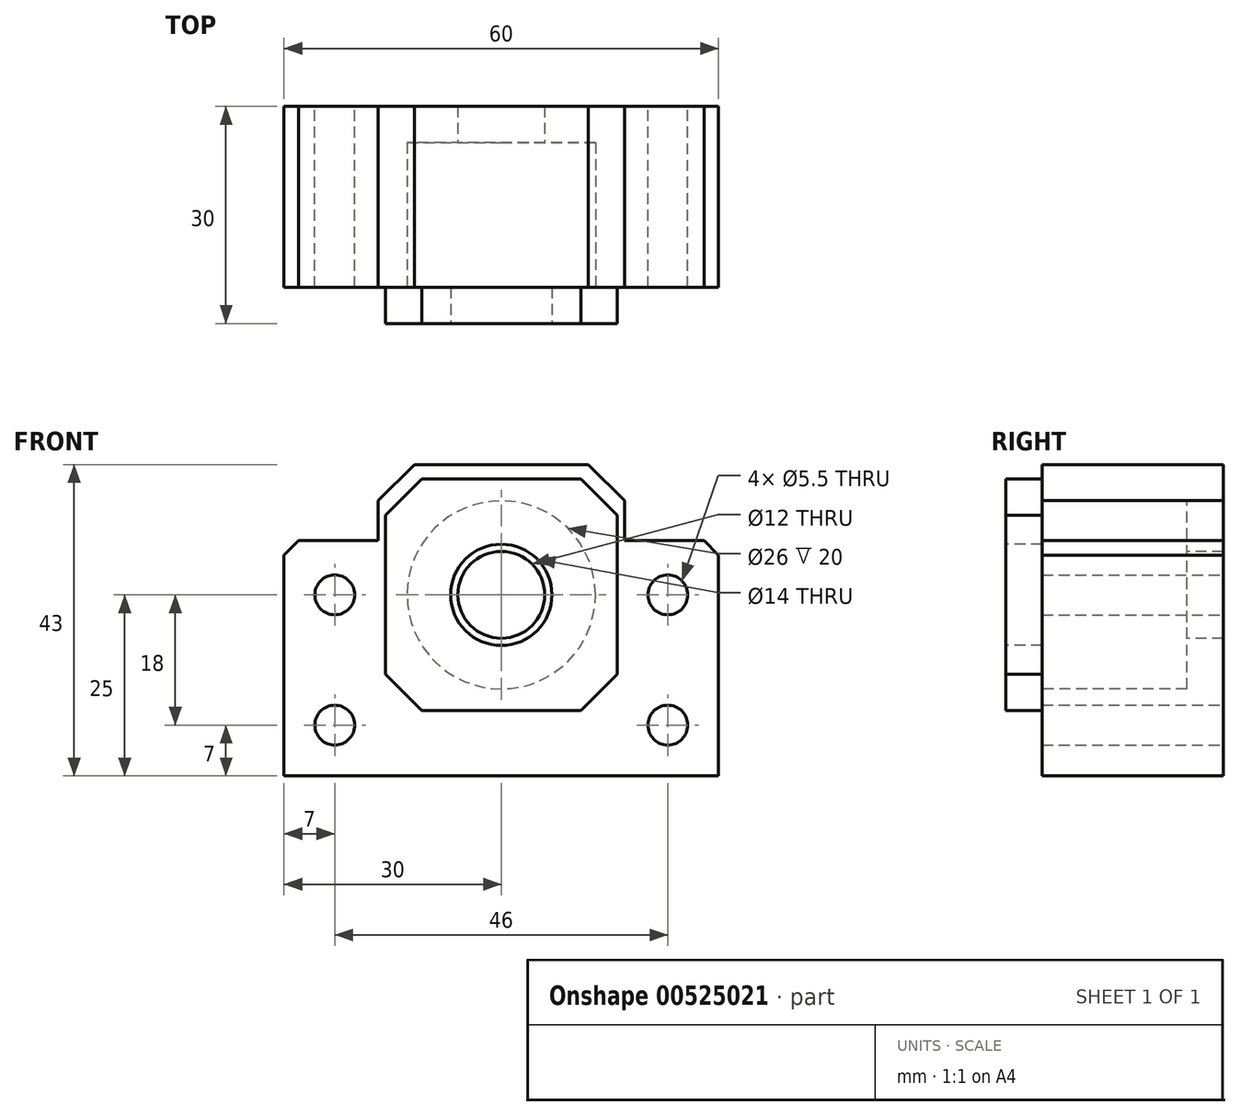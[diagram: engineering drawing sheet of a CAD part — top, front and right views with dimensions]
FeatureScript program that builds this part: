
annotation { "Feature Type Name" : "Feature", "Feature Type Description" : "" }
export const myFeature = defineFeature(function(context is Context, id is Id, definition is map)
    precondition{}
    {
        {
            var Q0;
            Q0=qCreatedBy(makeId("Front.planeOp"),FACE);
            var sketch = newSketch(context, id + "F0", { "sketchPlane" : qUnion([Q0])});
            skLineSegment(sketch, "E0.bottom", {"start": v(17, 21.5) * mm, "end": v(-17, 21.5) * mm});
            skLineSegment(sketch, "E0.top", {"start": v(30, -21.5) * mm, "end": v(-30, -21.5) * mm});
            skLineSegment(sketch, "E0.left", {"start": v(30, 11) * mm, "end": v(30, -21.5) * mm});
            skLineSegment(sketch, "E0.right", {"start": v(-30, 11) * mm, "end": v(-30, -21.5) * mm});
            skPoint(sketch, "E0.middle", {"position": v(0, 0) * mm});
            skLineSegment(sketch, "E1", {"start": v(-17, 21.5) * mm, "end": v(-17, 11) * mm});
            skLineSegment(sketch, "E2", {"start": v(-17, 11) * mm, "end": v(-30, 11) * mm});
            skLineSegment(sketch, "E3", {"start": v(17, 21.5) * mm, "end": v(17, 11) * mm});
            skLineSegment(sketch, "E4", {"start": v(17, 11) * mm, "end": v(30, 11) * mm});
            skPoint(sketch, "E5.orphan", {"position": v(-30, 21.5) * mm});
            skPoint(sketch, "E6.orphan", {"position": v(30, 21.5) * mm});
            skSolve(sketch);
        }
        {
            var Q0;
            Q0 = qSketchRegion(id + "F0", true);
            extrude(context, id + "F1", {"entities" : qUnion([Q0]), "endBound" : BoundingType.SYMMETRIC, "depth" : 25 * mm, "offsetDistance" : 25 * mm});
        }
        {
            var Q0;
            Q0=makeQuery(id+"F1.opExtrude","CAP_FACE",FACE,{"disambiguationData":[OSD([sQuery(id+"F0.wireOp",EDGE,"E0.bottom"),sQuery(id+"F0.wireOp",EDGE,"E0.top"),sQuery(id+"F0.wireOp",EDGE,"E0.left"),sQuery(id+"F0.wireOp",EDGE,"E0.right"),sQuery(id+"F0.wireOp",EDGE,"E1"),sQuery(id+"F0.wireOp",EDGE,"E2"),sQuery(id+"F0.wireOp",EDGE,"E3"),sQuery(id+"F0.wireOp",EDGE,"E4")])],"isStart":false});
            var sketch = newSketch(context, id + "F2", { "sketchPlane" : qUnion([Q0])});
            skCircle(sketch, "E7", {"center": v(0, 3.5) * mm, "radius": 6 * mm});
            skSolve(sketch);
        }
        {
            var Q0;
            Q0 = qSketchRegion(id + "F2", true);
            extrude(context, id + "F3", {"entities" : qUnion([Q0]), "operationType" : NewBodyOperationType.REMOVE, "oppositeDirection" : true, "depth" : 25 * mm, "offsetDistance" : 25 * mm});
        }
        {
            var Q0;
            Q0=makeQuery(id+"F1.opExtrude","CAP_FACE",FACE,{"disambiguationData":[OSD([sQuery(id+"F0.wireOp",EDGE,"E0.bottom"),sQuery(id+"F0.wireOp",EDGE,"E0.top"),sQuery(id+"F0.wireOp",EDGE,"E0.left"),sQuery(id+"F0.wireOp",EDGE,"E0.right"),sQuery(id+"F0.wireOp",EDGE,"E1"),sQuery(id+"F0.wireOp",EDGE,"E2"),sQuery(id+"F0.wireOp",EDGE,"E3"),sQuery(id+"F0.wireOp",EDGE,"E4")])],"isStart":false});
            var sketch = newSketch(context, id + "F4", { "sketchPlane" : qUnion([Q0])});
            skCircle(sketch, "E8", {"center": v(0, 3.5) * mm, "radius": 13 * mm});
            skSolve(sketch);
        }
        {
            var Q0;
            Q0 = qSketchRegion(id + "F4", true);
            extrude(context, id + "F5", {"entities" : qUnion([Q0]), "operationType" : NewBodyOperationType.REMOVE, "oppositeDirection" : true, "depth" : 20 * mm, "offsetDistance" : 25 * mm});
        }
        {
            var Q0;
            Q0=makeQuery(id+"F1.opExtrude","CAP_FACE",FACE,{"disambiguationData":[OSD([sQuery(id+"F0.wireOp",EDGE,"E0.bottom"),sQuery(id+"F0.wireOp",EDGE,"E0.top"),sQuery(id+"F0.wireOp",EDGE,"E0.left"),sQuery(id+"F0.wireOp",EDGE,"E0.right"),sQuery(id+"F0.wireOp",EDGE,"E1"),sQuery(id+"F0.wireOp",EDGE,"E2"),sQuery(id+"F0.wireOp",EDGE,"E3"),sQuery(id+"F0.wireOp",EDGE,"E4")])],"isStart":false});
            var sketch = newSketch(context, id + "F6", { "sketchPlane" : qUnion([Q0])});
            skLineSegment(sketch, "E9.bottom", {"start": v(16, -12.5) * mm, "end": v(-16, -12.5) * mm});
            skLineSegment(sketch, "E9.top", {"start": v(16, 19.5) * mm, "end": v(-16, 19.5) * mm});
            skLineSegment(sketch, "E9.left", {"start": v(16, -12.5) * mm, "end": v(16, 19.5) * mm});
            skLineSegment(sketch, "E9.right", {"start": v(-16, -12.5) * mm, "end": v(-16, 19.5) * mm});
            skPoint(sketch, "E9.middle", {"position": v(0, 3.5) * mm});
            skSolve(sketch);
        }
        {
            var Q0;
            Q0 = qSketchRegion(id + "F6", true);
            extrude(context, id + "F7", {"entities" : qUnion([Q0]), "operationType" : NewBodyOperationType.ADD, "depth" : 5 * mm, "offsetDistance" : 25 * mm});
        }
        {
            var Q0;
            Q0=makeQuery(id+"F7.opExtrude","CAP_FACE",FACE,{"disambiguationData":[OSD([sQuery(id+"F6.wireOp",EDGE,"E9.bottom"),sQuery(id+"F6.wireOp",EDGE,"E9.top"),sQuery(id+"F6.wireOp",EDGE,"E9.left"),sQuery(id+"F6.wireOp",EDGE,"E9.right")])],"isStart":false});
            var sketch = newSketch(context, id + "F8", { "sketchPlane" : qUnion([Q0])});
            skCircle(sketch, "E10", {"center": v(0, 3.5) * mm, "radius": 7 * mm});
            skSolve(sketch);
        }
        {
            var Q0;
            Q0 = qSketchRegion(id + "F8", true);
            extrude(context, id + "F9", {"entities" : qUnion([Q0]), "operationType" : NewBodyOperationType.REMOVE, "oppositeDirection" : true, "depth" : 5 * mm, "offsetDistance" : 25 * mm});
        }
        {
            var Q0;
            Q0=makeQuery(id+"F7.opExtrude","SWEPT_EDGE",EDGE,{"disambiguationData":[OSD([sQuery(id+"F6.wireOp",EDGE,"E9.top"),sQuery(id+"F6.wireOp",EDGE,"E9.right")])]});
            var Q1;
            Q1=makeQuery(id+"F7.opExtrude","SWEPT_EDGE",EDGE,{"disambiguationData":[OSD([sQuery(id+"F6.wireOp",EDGE,"E9.bottom"),sQuery(id+"F6.wireOp",EDGE,"E9.right")])]});
            var Q2;
            Q2=makeQuery(id+"F7.opExtrude","SWEPT_EDGE",EDGE,{"disambiguationData":[OSD([sQuery(id+"F6.wireOp",EDGE,"E9.top"),sQuery(id+"F6.wireOp",EDGE,"E9.left")])]});
            var Q3;
            Q3=makeQuery(id+"F7.opExtrude","SWEPT_EDGE",EDGE,{"disambiguationData":[OSD([sQuery(id+"F6.wireOp",EDGE,"E9.bottom"),sQuery(id+"F6.wireOp",EDGE,"E9.left")])]});
            chamfer(context, id + "F10", {"entities" : qUnion([Q0, Q1, Q2, Q3]), "width" : 5 * mm, "tangentPropagation" : true});
        }
        {
            var Q0;
            Q0=makeQuery(id+"F1.opExtrude","SWEPT_EDGE",EDGE,{"disambiguationData":[OSD([sQuery(id+"F0.wireOp",EDGE,"E0.bottom"),sQuery(id+"F0.wireOp",EDGE,"E3")])]});
            var Q1;
            Q1=makeQuery(id+"F1.opExtrude","SWEPT_EDGE",EDGE,{"disambiguationData":[OSD([sQuery(id+"F0.wireOp",EDGE,"E0.bottom"),sQuery(id+"F0.wireOp",EDGE,"E1")])]});
            chamfer(context, id + "F11", {"entities" : qUnion([Q0, Q1]), "width" : 5 * mm, "tangentPropagation" : true});
        }
        {
            var Q0;
            Q0=makeQuery(id+"F1.opExtrude","CAP_FACE",FACE,{"disambiguationData":[OSD([sQuery(id+"F0.wireOp",EDGE,"E0.bottom"),sQuery(id+"F0.wireOp",EDGE,"E0.top"),sQuery(id+"F0.wireOp",EDGE,"E0.left"),sQuery(id+"F0.wireOp",EDGE,"E0.right"),sQuery(id+"F0.wireOp",EDGE,"E1"),sQuery(id+"F0.wireOp",EDGE,"E2"),sQuery(id+"F0.wireOp",EDGE,"E3"),sQuery(id+"F0.wireOp",EDGE,"E4")])],"isStart":true});
            var sketch = newSketch(context, id + "F12", { "sketchPlane" : qUnion([Q0])});
            skCircle(sketch, "E11", {"center": v(-23, 3.5) * mm, "radius": 2.75 * mm});
            skCircle(sketch, "E12", {"center": v(23, 3.5) * mm, "radius": 2.75 * mm});
            skCircle(sketch, "E13", {"center": v(23, -14.5) * mm, "radius": 2.75 * mm});
            skCircle(sketch, "E14", {"center": v(-23, -14.5) * mm, "radius": 2.75 * mm});
            skSolve(sketch);
        }
        {
            var Q0;
            Q0 = qSketchRegion(id + "F12", true);
            extrude(context, id + "F13", {"entities" : qUnion([Q0]), "operationType" : NewBodyOperationType.REMOVE, "oppositeDirection" : true, "depth" : 25 * mm, "offsetDistance" : 25 * mm});
        }
        {
            var Q0;
            Q0=makeQuery(id+"F1.opExtrude","SWEPT_EDGE",EDGE,{"disambiguationData":[OSD([sQuery(id+"F0.wireOp",EDGE,"E0.left"),sQuery(id+"F0.wireOp",EDGE,"E4")])]});
            var Q1;
            Q1=makeQuery(id+"F1.opExtrude","SWEPT_EDGE",EDGE,{"disambiguationData":[OSD([sQuery(id+"F0.wireOp",EDGE,"E0.right"),sQuery(id+"F0.wireOp",EDGE,"E2")])]});
            chamfer(context, id + "F14", {"entities" : qUnion([Q0, Q1]), "width" : 2 * mm, "tangentPropagation" : true});
        }
    });
